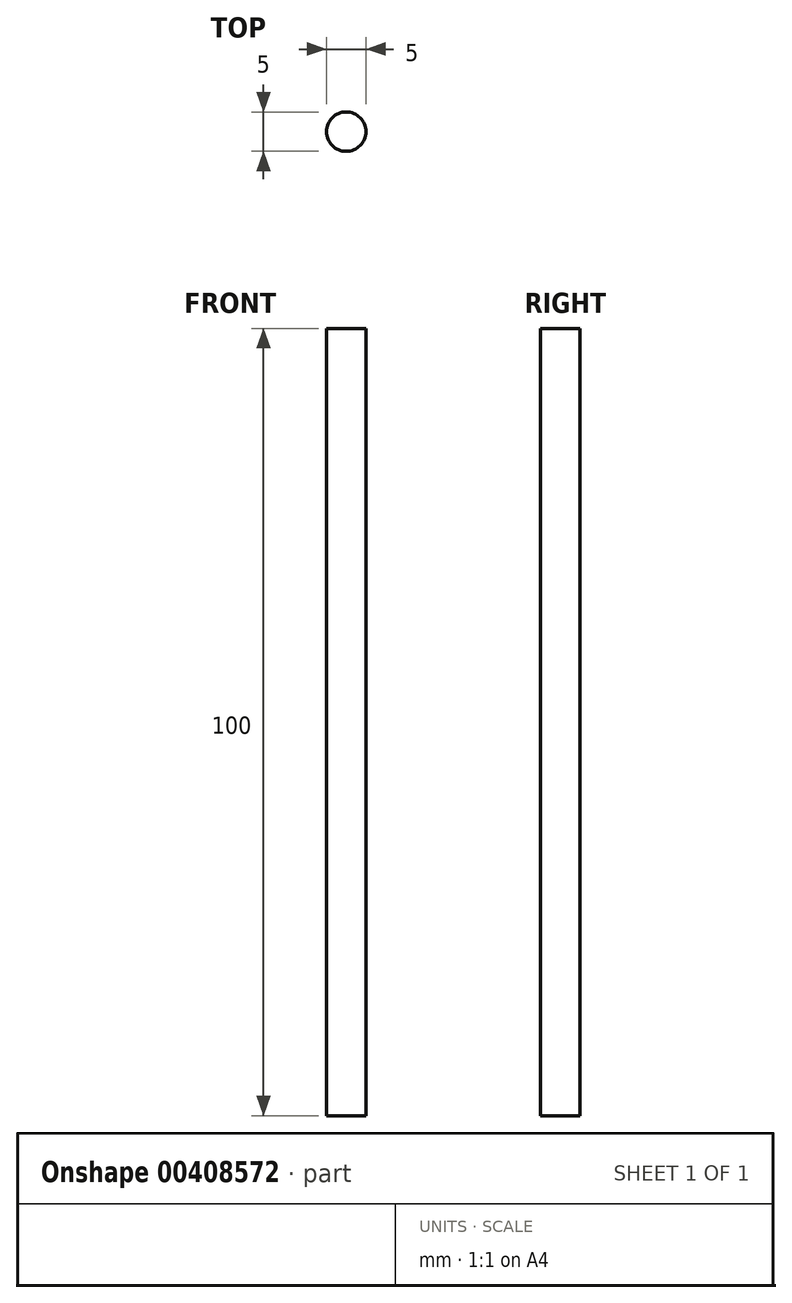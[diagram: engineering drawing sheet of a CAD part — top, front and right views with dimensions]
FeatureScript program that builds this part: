
annotation { "Feature Type Name" : "Feature", "Feature Type Description" : "" }
export const myFeature = defineFeature(function(context is Context, id is Id, definition is map)
    precondition{}
    {
        {
            var Q0;
            Q0=qCreatedBy(makeId("Top.planeOp"),FACE);
            var sketch = newSketch(context, id + "F0", { "sketchPlane" : qUnion([Q0])});
            skCircle(sketch, "E0", {"center": v(0, 0) * mm, "radius": 2.5 * mm});
            skSolve(sketch);
        }
        {
            var Q0;
            Q0 = qSketchRegion(id + "F0", true);
            extrude(context, id + "F1", {"entities" : qUnion([Q0]), "depth" : 100 * mm, "offsetDistance" : 25 * mm});
        }
    });
